# Revit family: НЕВАТОМ_Вентилятор VKRF, версия 1
name_source: partatom
category: Оборудование
revit_build: Autodesk Revit 2017 (Build: 20170118_1100(x64)
units: mm (PartAtom-declared; Revit-internal decimal feet)

## family parameters
Всегда вертикально = Да
На основе рабочей плоскости = Нет
Общий = Нет
При загрузке вырезать с полостями = Нет
Размер круглого соединителя = Использовать диаметр
Тип детали = Нормальный
Точка расчета площади = Нет

## types (42) — shared parameters
ADSK_Единица измерения = шт.
ADSK_Завод-изготовитель = НЕВАТОМ
ADSK_Количество = 1
ADSK_Материал наименование = Оцинкованная сталь
ADSK_Наименование = Вентилятор крышный радиальный с выбросом вверх
ADSK_Напряжение = 380 В
Nevatom_URL = https://t.me
Ключевая пометка = Вентиляция
Материал = Сталь ASTM A441
Мощность двигателя N, кВт = 55 кВт

## per-type parameters (varying)
| type | ADSK_Марка | ADSK_Масса | ADSK_Размер_Высота | ADSK_Размер_Длина | ADSK_Размер_Ширина | ADSK_Ток | ADSK_Частота вращения вентилятора | B | D | H | H1 | H2 | H3 | L | L1 | h | h1 | l | l1 | l2 | l3 |
| VKRF № 3,15 АИР63A4 | VKRF-3,15-0,25/1500 | 36.7 | 565 мм | 520 мм | 520 мм | 1 А | 1500 | 440 мм | 315 мм | 565 мм | 339 мм | 68 мм | 322 мм | 520 мм | 780 мм | 20 мм | 17 мм | 420 мм | 210 мм | 210 мм | 357 мм |
| VKRF № 12,5 АИР225M8 | VKRF-12,5-30,0/750 | 921.3 | 1690 мм | 1650 мм | 1650 мм | 64 А | 750 | 1550 мм | 1250 мм | 1690 мм | 1014 мм | 203 мм | 963 мм | 1650 мм | 2890 мм | 40 мм | 51 мм | 1550 мм | 775 мм | 775 мм | 1318 мм |
| VKRF № 3,15 АИР80B2 | VKRF-3,15-2,2/3000 | 47 | 565 мм | 520 мм | 520 мм | 5 А | 3000 | 440 мм | 315 мм | 565 мм | 339 мм | 68 мм | 322 мм | 520 мм | 780 мм | 20 мм | 17 мм | 420 мм | 210 мм | 210 мм | 357 мм |
| VKRF № 4 АИР63B6 | VKRF-4,0-0,25/1000 | 63 | 690 мм | 625 мм | 625 мм | 1 А | 1000 | 530 мм | 400 мм | 690 мм | 414 мм | 83 мм | 393 мм | 625 мм | 975 мм | 20 мм | 21 мм | 525 мм | 263 мм | 263 мм | 446 мм |
| VKRF № 4 АИР71B4 | VKRF № 4 АИР71B4 | 62.4 | 690 мм | 625 мм | 625 мм | 2 А | 1500 | 530 мм | 400 мм | 690 мм | 414 мм | 83 мм | 393 мм | 625 мм | 975 мм | 20 мм | 21 мм | 525 мм | 263 мм | 263 мм | 446 мм |
| VKRF № 4 АИР100L2 | VKRF-4,0-5,5/3000 | 84.5 | 690 мм | 625 мм | 625 мм | 11 А | 3000 | 530 мм | 400 мм | 690 мм | 414 мм | 83 мм | 393 мм | 625 мм | 975 мм | 20 мм | 21 мм | 525 мм | 263 мм | 263 мм | 446 мм |
| VKRF № 5 АИР80A6 | VKRF-5,0-0,75/1000 | 84.6 | 755 мм | 710 мм | 710 мм | 2 А | 1000 | 630 мм | 500 мм | 755 мм | 453 мм | 91 мм | 430 мм | 710 мм | 1190 мм | 20 мм | 23 мм | 610 мм | 305 мм | 305 мм | 519 мм |
| VKRF № 5 АИР90L4 | VKRF-5,0-2,2/1500 | 92 | 755 мм | 710 мм | 710 мм | 5 А | 1500 | 630 мм | 500 мм | 755 мм | 453 мм | 91 мм | 430 мм | 710 мм | 1190 мм | 20 мм | 23 мм | 610 мм | 305 мм | 305 мм | 519 мм |
| VKRF № 6,3 АИР100L6 | VKRF-6,3-2,2/1000 | 143.1 | 940 мм | 850 мм | 850 мм | 6 А | 1000 | 755 мм | 630 мм | 940 мм | 564 мм | 113 мм | 536 мм | 850 мм | 1445 мм | 20 мм | 28 мм | 750 мм | 375 мм | 375 мм | 638 мм |
| VKRF № 6,3 АИР132S4 | VKRF-6,3-7,5/1500 | 188 | 940 мм | 850 мм | 850 мм | 16 А | 1500 | 755 мм | 630 мм | 940 мм | 564 мм | 113 мм | 536 мм | 850 мм | 1445 мм | 20 мм | 28 мм | 750 мм | 375 мм | 375 мм | 638 мм |
| VKRF № 8 АИР112MB8 | VKRF-8,0-3,0/750 | 258 | 1260 мм | 1080 мм | 1080 мм | 8 А | 750 | 1005 мм | 800 мм | 1260 мм | 756 мм | 151 мм | 718 мм | 1080 мм | 1875 мм | 20 мм | 38 мм | 980 мм | 490 мм | 490 мм | 833 мм |
| VKRF № 8 АИР132M6 | VKRF-8,0-7,5/1000 | 292 | 1260 мм | 1080 мм | 1080 мм | 17 А | 1000 | 1005 мм | 800 мм | 1260 мм | 756 мм | 151 мм | 718 мм | 1080 мм | 1875 мм | 20 мм | 38 мм | 980 мм | 490 мм | 490 мм | 833 мм |
| VKRF № 8 АИР180S4 | VKRF-8,0-22,0/1500 | 379 | 1260 мм | 1080 мм | 1080 мм | 43 А | 1500 | 1005 мм | 800 мм | 1260 мм | 756 мм | 151 мм | 718 мм | 1080 мм | 1875 мм | 20 мм | 38 мм | 980 мм | 490 мм | 490 мм | 833 мм |
| VKRF № 10 АИР160M8 | VKRF-10-11/750 | 524 | 1480 мм | 1500 мм | 1500 мм | 26 А | 750 | 1389 мм | 1000 мм | 1480 мм | 888 мм | 178 мм | 844 мм | 1500 мм | 2490 мм | 20 мм | 44 мм | 1400 мм | 700 мм | 700 мм | 1190 мм |
| VKRF № 10 АИР200M6 | VKRF-10,0-22,0/1000 | 614 | 1480 мм | 1500 мм | 1500 мм | 44 А | 1000 | 1389 мм | 1000 мм | 1480 мм | 888 мм | 178 мм | 844 мм | 1500 мм | 2490 мм | 20 мм | 44 мм | 1400 мм | 700 мм | 700 мм | 1190 мм |
| VKRF № 3,55 АИР63В4 | VKRF-3,55-0,37/1500 | 46.9 | 620 мм | 555 мм | 555 мм | 1 А | 1500 | 480 мм | 355 мм | 620 мм | 372 мм | 74 мм | 353 мм | 555 мм | 806 мм | 20 мм | 19 мм | 455 мм | 228 мм | 228 мм | 387 мм |
| VKRF № 4,5 АИР71А6 | VKRF-4,5-0,37/1000 | 70.1 | 872 мм | 655 мм | 655 мм | 1 А | 1000 | 580 мм | 450 мм | 872 мм | 523 мм | 105 мм | 497 мм | 655 мм | 1004 мм | 20 мм | 26 мм | 555 мм | 278 мм | 278 мм | 472 мм |
| VKRF № 5,6 АИР80B6 | VKRF-5,6-1,1/1000 | 103 | 795 мм | 765 мм | 765 мм | 3 А | 1000 | 690 мм | 560 мм | 795 мм | 477 мм | 95 мм | 453 мм | 765 мм | 1242 мм | 20 мм | 24 мм | 665 мм | 333 мм | 333 мм | 565 мм |
| VKRF № 7,1 АИР112MA8 | VKRF-7,1-2,2/750 | 269.5 | 1227 мм | 920 мм | 920 мм | 6 А | 750 | 840 мм | 710 мм | 1227 мм | 736 мм | 147 мм | 699 мм | 920 мм | 1614 мм | 20 мм | 37 мм | 820 мм | 410 мм | 410 мм | 697 мм |
| VKRF № 3,15 АИР56А4 | VKRF-3,15-0,12/1500 | 35.4 | 565 мм | 520 мм | 520 мм | 0 А | 1500 | 440 мм | 315 мм | 565 мм | 339 мм | 68 мм | 322 мм | 520 мм | 780 мм | 20 мм | 17 мм | 420 мм | 210 мм | 210 мм | 357 мм |
| VKRF № 3,15 АИР71В2 | VKRF-3,15-1,1/3000 | 41.3 | 565 мм | 520 мм | 520 мм | 3 А | 3000 | 440 мм | 315 мм | 565 мм | 339 мм | 68 мм | 322 мм | 520 мм | 780 мм | 20 мм | 17 мм | 420 мм | 210 мм | 210 мм | 357 мм |
| VKRF № 3,55 АИР90L2 | VKRF-3,55-3,0/3000 | 62.1 | 620 мм | 555 мм | 555 мм | 6 А | 3000 | 480 мм | 355 мм | 620 мм | 372 мм | 74 мм | 353 мм | 555 мм | 806 мм | 20 мм | 19 мм | 455 мм | 228 мм | 228 мм | 387 мм |
| VKRF № 4 АИР90L2 | VKRF-4,0-3,0/3000 | 72 | 690 мм | 625 мм | 625 мм | 6 А | 3000 | 530 мм | 400 мм | 690 мм | 414 мм | 83 мм | 393 мм | 625 мм | 975 мм | 20 мм | 21 мм | 525 мм | 263 мм | 263 мм | 446 мм |
| VKRF № 4 АИР63В4 | VKRF-4,0-0,37/1500 | 58.6 | 690 мм | 625 мм | 625 мм | 1 А | 1500 | 530 мм | 400 мм | 690 мм | 414 мм | 83 мм | 393 мм | 625 мм | 975 мм | 20 мм | 21 мм | 525 мм | 263 мм | 263 мм | 446 мм |
| VKRF № 4,5 АИР80В4 | VKRF-4,5-1,5/1500 | 78.1 | 872 мм | 655 мм | 655 мм | 4 А | 1500 | 580 мм | 450 мм | 872 мм | 523 мм | 105 мм | 497 мм | 655 мм | 1004 мм | 20 мм | 26 мм | 555 мм | 278 мм | 278 мм | 472 мм |
| VKRF № 4,5 АИР132М2 | VKRF-4,5-11/3000 | 141.4 | 872 мм | 655 мм | 655 мм | 21 А | 3000 | 580 мм | 450 мм | 872 мм | 523 мм | 105 мм | 497 мм | 655 мм | 1004 мм | 20 мм | 26 мм | 555 мм | 278 мм | 278 мм | 472 мм |
| VKRF № 5 АИР71А6 | VKRF-5,0-0,37/1000 | 80.4 | 755 мм | 710 мм | 710 мм | 1 А | 1000 | 630 мм | 500 мм | 755 мм | 453 мм | 91 мм | 430 мм | 710 мм | 1190 мм | 20 мм | 23 мм | 610 мм | 305 мм | 305 мм | 519 мм |
| VKRF № 5 АИР80В4 | VKRF-5,0-1,5/1500 | 87 | 755 мм | 710 мм | 710 мм | 4 А | 1500 | 630 мм | 500 мм | 755 мм | 453 мм | 91 мм | 430 мм | 710 мм | 1190 мм | 20 мм | 23 мм | 610 мм | 305 мм | 305 мм | 519 мм |
| VKRF № 5 АИР132М2 | VKRF-5,0-11,0/3000 | 143 | 755 мм | 710 мм | 710 мм | 21 А | 3000 | 630 мм | 500 мм | 755 мм | 453 мм | 91 мм | 430 мм | 710 мм | 1190 мм | 20 мм | 23 мм | 610 мм | 305 мм | 305 мм | 519 мм |
| VKRF № 5,6 АИР100L4 | VKRF-5,6-4,0/1500 | 112 | 795 мм | 765 мм | 765 мм | 9 А | 1500 | 690 мм | 560 мм | 795 мм | 477 мм | 95 мм | 453 мм | 765 мм | 1242 мм | 20 мм | 24 мм | 665 мм | 333 мм | 333 мм | 565 мм |
| VKRF № 6,3 АИР80В6 | VKRF-6,3-1,1/1000 | 131 | 940 мм | 850 мм | 850 мм | 3 А | 1000 | 755 мм | 630 мм | 940 мм | 564 мм | 113 мм | 536 мм | 850 мм | 1445 мм | 20 мм | 28 мм | 750 мм | 375 мм | 375 мм | 638 мм |
| VKRF № 6,3 АИР100L4 | VKRF-6,3-4,0/1500 | 147 | 940 мм | 850 мм | 850 мм | 9 А | 1500 | 755 мм | 630 мм | 940 мм | 564 мм | 113 мм | 536 мм | 850 мм | 1445 мм | 20 мм | 28 мм | 750 мм | 375 мм | 375 мм | 638 мм |
| VKRF № 7,1 АИР112МВ6 | VKRF-7,1-4,0/1000 | 274 | 1227 мм | 920 мм | 920 мм | 9 А | 1000 | 840 мм | 710 мм | 1227 мм | 736 мм | 147 мм | 699 мм | 920 мм | 1614 мм | 20 мм | 37 мм | 820 мм | 410 мм | 410 мм | 697 мм |
| VKRF № 7,1 АИР160S4 | VKRF-7,1-15,0/1500 | 333 | 1227 мм | 920 мм | 920 мм | 30 А | 1500 | 840 мм | 710 мм | 1227 мм | 736 мм | 147 мм | 699 мм | 920 мм | 1614 мм | 20 мм | 37 мм | 820 мм | 410 мм | 410 мм | 697 мм |
| VKRF № 8 АИР112МВ6 | VKRF-8,0-4,0/1000 | 254 | 1260 мм | 1080 мм | 1080 мм | 9 А | 1000 | 1005 мм | 800 мм | 1260 мм | 756 мм | 151 мм | 718 мм | 1080 мм | 1875 мм | 20 мм | 38 мм | 980 мм | 490 мм | 490 мм | 833 мм |
| VKRF № 8 АИР160S4 | VKRF-8,0-15,0/1500 | 335 | 1260 мм | 1080 мм | 1080 мм | 30 А | 1500 | 1005 мм | 800 мм | 1260 мм | 756 мм | 151 мм | 718 мм | 1080 мм | 1875 мм | 20 мм | 38 мм | 980 мм | 490 мм | 490 мм | 833 мм |
| VKRF № 10 АИР132М8 | VKRF-10,0-5,5/750 | 460 | 1480 мм | 1500 мм | 1500 мм | 14 А | 750 | 1389 мм | 1000 мм | 1480 мм | 888 мм | 178 мм | 844 мм | 1500 мм | 2490 мм | 20 мм | 44 мм | 1400 мм | 700 мм | 700 мм | 1190 мм |
| VKRF № 10 АИР160S6 | VKRF-10,0-11,0/1000 | 499 | 1480 мм | 1500 мм | 1500 мм | 24 А | 1000 | 1389 мм | 1000 мм | 1480 мм | 888 мм | 178 мм | 844 мм | 1500 мм | 2490 мм | 20 мм | 44 мм | 1400 мм | 700 мм | 700 мм | 1190 мм |
| VKRF № 10 АИР200М4 | VKRF-10,0-37,0/1500 | 640 | 1480 мм | 1500 мм | 1500 мм | 69 А | 1500 | 1389 мм | 1000 мм | 1480 мм | 888 мм | 178 мм | 844 мм | 1500 мм | 2490 мм | 20 мм | 44 мм | 1400 мм | 700 мм | 700 мм | 1190 мм |
| VKRF № 12,5 АИР250М6 | VKRF-12,5-55,0/1000 | 1104 | 1690 мм | 1650 мм | 1650 мм | 103 А | 1000 | 1550 мм | 1250 мм | 1690 мм | 1014 мм | 203 мм | 963 мм | 1650 мм | 2890 мм | 40 мм | 51 мм | 1550 мм | 775 мм | 775 мм | 1318 мм |
| VKRF № 12,5 АИР180М8 | VKRF-12,5-15,0/750 | 788 | 1690 мм | 1650 мм | 1650 мм | 35 А | 750 | 1550 мм | 1250 мм | 1690 мм | 1014 мм | 203 мм | 963 мм | 1650 мм | 2890 мм | 40 мм | 51 мм | 1550 мм | 775 мм | 775 мм | 1318 мм |
| VKRF № 12,5 АИР225М6 | VKRF-12,5-37,0/1000 | 915.3 | 1690 мм | 1650 мм | 1650 мм | 71 А | 1000 | 1550 мм | 1250 мм | 1690 мм | 1014 мм | 203 мм | 963 мм | 1650 мм | 2890 мм | 40 мм | 51 мм | 1550 мм | 775 мм | 775 мм | 1318 мм |
